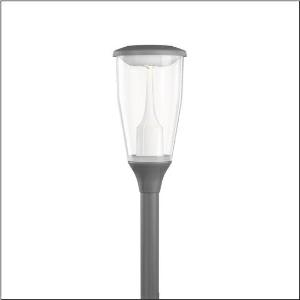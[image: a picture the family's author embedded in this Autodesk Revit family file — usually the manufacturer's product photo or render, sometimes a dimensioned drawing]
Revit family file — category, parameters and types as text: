
# Revit family: dl_11_iq___p1_0a_5xa5575ff14h000022_b904
name_source: partatom
category: Lighting Fixtures
units: mm (PartAtom-declared; Revit-internal decimal feet)

## family parameters
Cut with Voids When Loaded = No
Host = Face
Light Source = No
Part Type = Normal
Room Calculation Point = No
Round Connector Dimension = Use Diameter
Shared = No

## types (1)
- --- (1 x LED, 1530 lm, 10.5 W, 3000K)
    Apparent Load = 11 VA
    CIE Flux Codes = 34 63 91 95 100
    Color Rendering = 70
    Color Temperature = 3000K
    Default Elevation = 1800 mm
    Description = DL 11 iQ, mast luminaire, Module 540 iQ-SR, primary light control with 3 zone facetted reflector, of plastic, silver coated, highly specular, structured, primary optical cover: cover, of PMMA, transparent, light distribution: P1.0a, light emission: direct distribution, primary light characteristic: asymmetric, installation type: post-top, LED, High Power LED, rated luminous flux: 1.560lm, luminous efficacy: 149lm/W, light colour: 730, colour temperature: 3000K, control: Street-Remote, Auto-Match, Temp-Guard, Lumen-Switch, Night-Set, Smart-Wire, Light-Fading, Desk-Remote (wireless, voltage-free reading and setting of iQ features in the workshop via application-optimized NFC function/RFID function), optimised constant luminous flux control (CLO 2.0), mains connection: 220..240V, AC, 50/60Hz, connection cable pre-assembled, cable length: 5,5m, wiring characteristics: H07RN-F, 5-core, 1.5mm², start of lifetime: 10W, end of service life: 11W, reduction: 5W, luminaire housing, upper part, of diecast aluminium, coated, Siteco® metallic grey (DB 702S), spigot size: 76mm (post-top), post-top mast mounting element, of diecast aluminium, coated, Siteco® metallic grey (DB 702S), Module 540 iQ-SR, traffic white (RAL 9016), equipment: standard, protection rating (complete): IP66, insulation class (complete): insulation class II (safety insulation), certification: CE, ENEC, ENEC+, VDE, packaging unit: 1 piece

Light Distribution: P1.0a
    Height = 665 mm
    Lamp = 1 x LED
    Lamp Light Flux = 1530 lm
    Lamp Power = 10.5 W
    Lamp count = 1
    Length = 334 mm
    Luminous efficacy = 146 lm/W
    Manufacturer = Siteco
    ModVariant = No
    Model = 5XA5575FF14H000022
    Number of Poles = 1
    OnlyDefault = Yes
    Power Factor = 1
    Product Name = DL 11 iQ | P1.0a
    Product group = mast luminaire | pylon top
    ProductGroupID = 6100
    Protection Class = Protection class II
    Protection Degree = IP 66
    RLX_Detail_Level = 1
    RLX_Emergency_Light_Flux = 0 lm
    RLX_Emergency_Type = 0
    RLX_Emergency_Type_DB = No
    RlxData = <blob elided: 103281 chars, md5=f70c2085>
    Socket = socket
    Standby Power = 0 W
    System Light Flux = 1530 lm
    System Power = 11 W
    Type Comments = factory setting: luminous flux: 100 % | dim-lin: 254 | 419 mA
    Type Image = l_1258354.jpg
    URL = http://relux.com
    VarID = @adj_042307
    Voltage = 0 V
    Weight = 0.00 kg
    Width = 0 mm  [stored 0 ft]

note: [stored X ft] marks values corroborated as IEEE doubles in the binary element streams (Revit-internal decimal feet)

## geometry (parser evidence)
native form markers: Blend x4, Sweep x12
no freeform markers — native parametric forms only
